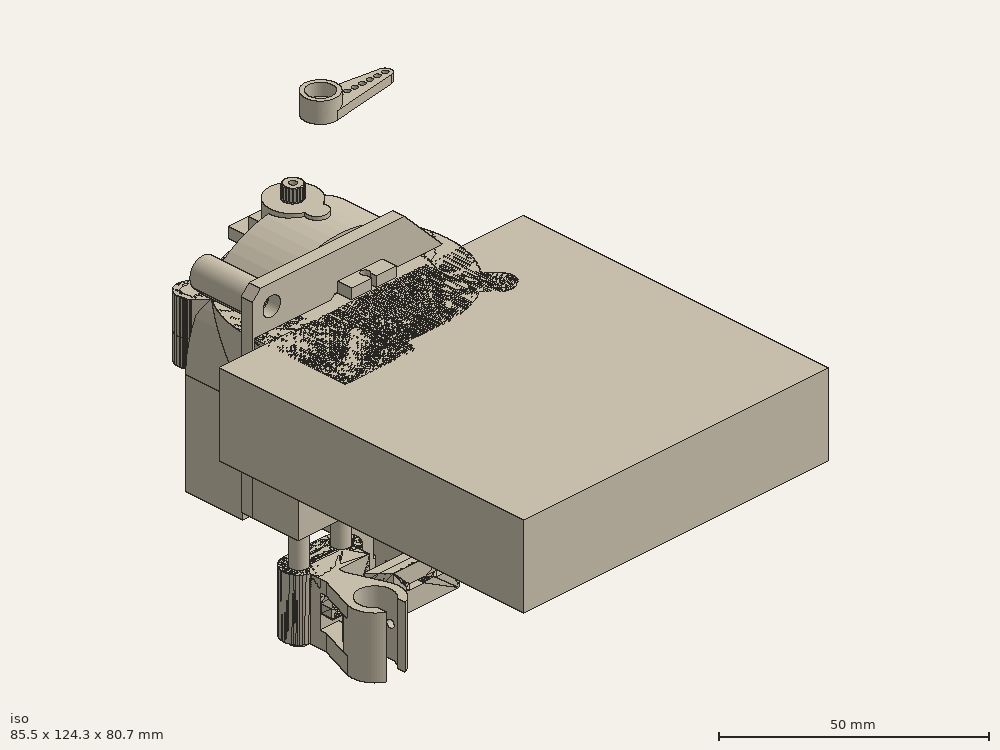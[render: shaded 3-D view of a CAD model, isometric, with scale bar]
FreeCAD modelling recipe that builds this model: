
FCSTD DOCUMENT  (FreeCAD 0.17R13522 (Git))
Label: plotter
License: All rights reserved
LicenseURL: http://en.wikipedia.org/wiki/All_rights_reserved
objects: Part::Box×15, Part::Cylinder×15, App::DocumentObjectGroup×11, Part::Cut×11, PartDesign::ShapeBinder×7, Part::Fuse×7, Sketcher::SketchObject×7, Part::MultiFuse×7, Part::Feature×6, Part::Chamfer×6, PartDesign::Point×5, Part::Part2DObjectPython×4, PartDesign::Pocket×4, Mesh::Feature×3, PartDesign::Pad×3, Part::Fillet×2, PartDesign::Body×2, Part::Compound×1, Spreadsheet::Sheet×1, Part::FeaturePython×1, +1 more types
note: 111 computed .brp shape members not serialized (recipe doc carries the construction recipe); baked Part::Feature solids carry a one-line shape summary decoded from their .brp

FEATURE [Part::Feature] Part__Feature  label="TFD-B5015 TITAN"
  Placement = pos=(0,0,7.5) rot=(0,0,1;0rad)
  shape: bbox 51.8 x 51.1 x 15 mm, 65 faces (baked)
FEATURE [Part::Feature] Part__Feature001  label="TFD-B5015 TITAN001"
  shape: bbox 43 x 43 x 11.5 mm, 91 faces (baked)
FEATURE [Part::Part2DObjectPython] Line  # Draft 2D object (typed FeaturePython)
  ChamferSize = 0
  Closed = false
  End = (0,0,10.5)
  FilletRadius = 0
  MakeFace = false
  MapMode = 5
  Points = (2) [(-2.07596,14.8557,11),(0,0,10.5)]
  Start = (-2.07596,14.8557,11)
  Support = -> [Part__Feature001]
FEATURE [Part::Part2DObjectPython] Line001  # Draft 2D object (typed FeaturePython)
  ChamferSize = 0
  Closed = false
  End = (4.6539,11.0608,10.5)
  FilletRadius = 0
  MakeFace = false
  MapMode = 5
  Points = (2) [(0,0,10.5),(4.6539,11.0608,10.5)]
  Start = (0,0,10.5)
  Support = -> [Part__Feature001]
FEATURE [Part::Fillet] Fillet
  Edges = 1 edges r=1: [Edge57]
FEATURE [App::DocumentObjectGroup] Group  label="Inner-part-src"
  Group = -> [Fillet]
FEATURE [Part::Feature] Fillet001  label="Inner-part-final"
  shape: bbox 43 x 43 x 11.5 mm, 153 faces (baked)
FEATURE [Part::Part2DObjectPython] Line002  # Draft 2D object (typed FeaturePython)
  ChamferSize = 0
  Closed = false
  End = (19.4,-18.3,15)
  FilletRadius = 0
  MakeFace = false
  MapMode = 5
  Points = (2) [(0,0,15),(19.4,-18.3,15)]
  Start = (0,0,15)
  Support = -> [Part__Feature]
FEATURE [Part::Part2DObjectPython] Line003  # Draft 2D object (typed FeaturePython)
  ChamferSize = 0
  Closed = false
  End = (-23.2,20.1,15)
  FilletRadius = 0
  MakeFace = false
  MapMode = 5
  Points = (2) [(0,0,15),(-23.2,20.1,15)]
  Start = (0,0,15)
  Support = -> [Part__Feature]
FEATURE [App::DocumentObjectGroup] Construction
  Group = -> [Line,Line001,Line002,Line003]
FEATURE [Part::Cut] Cut  label="cover-1"
  Refine = true
FEATURE [App::DocumentObjectGroup] Group001  label="cover-src"
  Group = -> [Cut]
FEATURE [Part::Feature] Pad005001  label="cover-final"
  Placement = pos=(0,0,-2) rot=(0,0,1;0rad)
  shape: bbox 51.8 x 51 x 15 mm, 33 faces (baked)
FEATURE [Part::Compound] Compound  label="Blower-50x50-final"
  Links = -> [Fillet001,Pad005001]
  Placement = pos=(0,15,0) rot=(1,0,0;1.5708rad)
FEATURE [App::DocumentObjectGroup] Group002  label="Blower"
  Group = -> [Part__Feature,Part__Feature001,Construction,Group,Group001,Compound]
FEATURE [Mesh::Feature] original
FEATURE [Part::Box] Box  label="Cubo"
  AttacherType = Attacher::AttachEngine3D
  Height = 20
  Length = 80
  Placement = pos=(-40,-84,-5) rot=(0,0,1;0rad)
  Width = 80
FEATURE [Mesh::Feature] difference
FEATURE [Mesh::Feature] union
  Placement = pos=(-23,50.7,-49.11) rot=(0,0,1;3.14159rad)
FEATURE [App::DocumentObjectGroup] Group003  label="Fan duct"
  Group = -> [original,Box,difference,union]
FEATURE [PartDesign::ShapeBinder] CopyCompound
  Placement = pos=(0,2,0) rot=(1,0,0;1.5708rad)
FEATURE [PartDesign::Point] DatumPoint  label="DatumPoint_MainScrew1"
  AttacherType = Attacher::AttachEnginePoint
  MapMode = 36
  Placement = pos=(-23.2,2,20.1) rot=(1,0,0;3.14159rad)
  Support = -> [CopyCompound]
FEATURE [PartDesign::ShapeBinder] CopyCompound001
  Placement = pos=(0,2,0) rot=(1,0,0;1.5708rad)
FEATURE [PartDesign::Point] DatumPoint001  label="DatumPoint_MainScrew2"
  AttacherType = Attacher::AttachEnginePoint
  MapMode = 36
  Placement = pos=(19.4,2,-18.3) rot=(1,0,0;3.14159rad)
  Support = -> [CopyCompound001]
FEATURE [Spreadsheet::Sheet] Spreadsheet
  cells = A2=Fan hole diameter; B2(fanHoleDiam)=32; A3=Fan support thickness; B3(FanSuppThick)=3; A4=Fan support width; B4(FanSuppWidth)=10; A5=Shaft thickness; B5(shaftThick)=4; A6=Left Shaft length; B6(shaftLength)=50; A7=Right shaft length; B7(shaftLengthRight)=33; A9=Shaft Axis X position; B9(AxisX)==-Spreadsheet.FanSuppWidth - 13; A10=Shaft Axis Y position; B10(AxisY)=-8; A12=Shaft Axis tolerance; B12(AxisTolerance)=0.20000000000000001; A13=Shaft Axis separation; B13(AxisSeparation)=11; A15=Servo Connecting Rod Flexible Part Thickness; B15(FlexThickness)=0.80000000000000004; A18=Agrandar el prisionero de M2 a M3; A19=Tornillos soporte principal M3; A20=Modificar parte flexible al doble de tamaño
FEATURE [Part::Box] Box001  label="Cubo001"
  AttacherType = Attacher::AttachEngine3D
  Height = 22.7
  Length = 11.8
  Width = 22.5
FEATURE [Part::Box] Box002  label="Cubo002"
  AttacherType = Attacher::AttachEngine3D
  Height = 2.5
  Length = 11.8
  Placement = pos=(0,-4.7,15.9) rot=(0,0,1;0rad)
  Width = 32.4
FEATURE [Part::Fuse] Fusion  label="Square_body"
  Base = -> Box001
  Refine = true
  Tool = -> Box002
FEATURE [Part::Cylinder] Cylinder  label="Cilindro"
  Angle = 360
  AttacherType = Attacher::AttachEngine3D
  Height = 4
  Placement = pos=(5.9,16.6,22.7) rot=(0,0,1;0rad)
  Radius = 5.9
FEATURE [Part::Cylinder] Cylinder001  label="Cilindro001"
  Angle = 360
  AttacherType = Attacher::AttachEngine3D
  Height = 4
  Placement = pos=(5.9,10.3,22.7) rot=(0,0,1;0rad)
  Radius = 2.5
FEATURE [Part::Fuse] Fusion001
  Base = -> Cylinder
  Refine = true
  Tool = -> Cylinder001
FEATURE [Part::Fuse] Fusion003
  Base = -> Fusion
  Refine = true
  Tool = -> Fusion001
FEATURE [Part::Cylinder] Cylinder003  label="Taladro"
  Angle = 360
  AttacherType = Attacher::AttachEngine3D
  Height = 10
  Placement = pos=(5.9,-2.35,11) rot=(0,0,1;0rad)
  Radius = 1
FEATURE [Part::Cylinder] Cylinder004  label="Taladro2"
  Angle = 360
  AttacherType = Attacher::AttachEngine3D
  Height = 10
  Placement = pos=(5.9,24.85,11) rot=(0,0,1;0rad)
  Radius = 1
FEATURE [Part::Fuse] Fusion004  label="Taladros"
  Base = -> Cylinder003
  Refine = true
  Tool = -> Cylinder004
FEATURE [Part::Box] Box003  label="Cubo003"
  AttacherType = Attacher::AttachEngine3D
  Height = 10
  Length = 1.3
  Placement = pos=(5.25,-6,12) rot=(0,0,1;0rad)
  Width = 3.3
FEATURE [Part::Box] Box004  label="Cubo004"
  AttacherType = Attacher::AttachEngine3D
  Height = 10
  Length = 1.3
  Placement = pos=(5.25,25,12) rot=(0,0,1;0rad)
  Width = 3.3
FEATURE [Part::Fuse] Fusion005  label="Rebajes"
  Base = -> Box003
  Refine = true
  Tool = -> Box004
FEATURE [Part::Fuse] Fusion006  label="Taladros001"
  Base = -> Fusion004
  Refine = true
  Tool = -> Fusion005
FEATURE [Part::Cut] Cut001  label="Cuerpo_con_taladros"
  Base = -> Fusion003
  Placement = pos=(-5.9,0,0) rot=(0,0,1;0rad)
  Refine = true
  Tool = -> Fusion006
FEATURE [Part::Cylinder] Cylinder006  label="Cilindro002"
  Angle = 360
  AttacherType = Attacher::AttachEngine3D
  Height = 3
  Placement = pos=(2.51021,16.5511,26.9) rot=(0,0,1;0rad)
  Radius = 0.35
FEATURE [Part::FeaturePython] Array  # Draft array (typed FeaturePython)
  Angle = 360
  ArrayType = 1
  Axis = (0,0,1)
  Base = -> Cylinder006
  Center = (0,16.6,0)
  Fuse = false
  IntervalAxis = (0,0,0)
  IntervalX = (1,0,0)
  IntervalY = (0,1,0)
  IntervalZ = (0,0,0)
  NumberPolar = 20
  NumberX = 2
  NumberY = 2
  NumberZ = 1
FEATURE [Part::Cylinder] Cylinder002  label="Cilindro_interior"
  Angle = 360
  AttacherType = Attacher::AttachEngine3D
  Height = 3.2
  Placement = pos=(0,16.6,26.7) rot=(0,0,1;0rad)
  Radius = 2.3
FEATURE [Part::Cylinder] Cylinder005  label="Cilindro_exterior"
  Angle = 360
  AttacherType = Attacher::AttachEngine3D
  Height = 3.2
  Placement = pos=(0,16.6,26.7) rot=(0,0,1;0rad)
  Radius = 0.85
FEATURE [Part::Cut] Cut002  label="Cilindro_vaciado"
  Base = -> Cylinder002
  Refine = true
  Tool = -> Cylinder005
FEATURE [Part::Fillet] Fillet002
  Base = -> Cut002
  Edges = 1 edges r=0.3: [Edge1]
FEATURE [Part::Cut] Cut003  label="Eje_engranaje"
  Base = -> Fillet002
  Refine = true
  Tool = -> Array
FEATURE [Part::Feature] Fusion007001  label="Servo-sg90-final"
  Placement = pos=(10,14.9,-22) rot=(0,0.707107,-0.707107;3.14159rad)
  shape: bbox 11.8 x 29.9 x 32.4 mm, 77 faces (baked)
  expr: Placement.Base.y = 17.899999999999999 - Spreadsheet.FanSuppThick
FEATURE [App::DocumentObjectGroup] Grupo003  label="Servo"
  Group = -> [Cut001,Cut003,Fusion007001]
FEATURE [Part::Fuse] Fusion008
  Placement = pos=(26.9697,36.3362,25.6722) rot=(0,0,1;0rad)
  Refine = true
FEATURE [App::DocumentObjectGroup] Grupo001  label="1-arm-horn"
  Group = -> [Fusion008]
FEATURE [Part::Feature] Pocket002001  label="Final-1-arm-horn"
  Placement = pos=(9.96971,-16.96,-38.6278) rot=(0,0.707107,0.707107;3.14159rad)
  shape: bbox 22.5 x 5 x 8 mm, 19 faces (baked)
  expr: Placement.Base.y = -13.960000000000001 - Spreadsheet.FanSuppThick
FEATURE [App::DocumentObjectGroup] Group004  label="ServoArm"
  Group = -> [Grupo001,Pocket002001]
FEATURE [PartDesign::ShapeBinder] CopyFusion007001
FEATURE [PartDesign::Point] DatumPoint002  label="DatumPoint_ServoHeight"
  AttacherType = Attacher::AttachEnginePoint
  MapMode = 37
  Placement = pos=(15.9,-8.8,-22) rot=(0,0,1;0rad)
  Support = -> [CopyFusion007001]
FEATURE [PartDesign::ShapeBinder] CopyFusion007001001
  Placement = pos=(15.9,13.9,-22) rot=(0,0.707107,-0.707107;3.14159rad)
FEATURE [PartDesign::Point] DatumPoint003  label="DatumPoint_ServoScrew1"
  AttacherType = Attacher::AttachEnginePoint
  MapMode = 36
  Placement = pos=(10,-4.5,-19.65) rot=(0,0,1;3.14159rad)
  Support = -> [CopyFusion007001001]
FEATURE [PartDesign::ShapeBinder] CopyFusion007001002
  Placement = pos=(15.9,13.9,-22) rot=(0,0.707107,-0.707107;3.14159rad)
FEATURE [PartDesign::Point] DatumPoint004  label="DatumPoint_ServoScrew2"
  AttacherType = Attacher::AttachEnginePoint
  MapMode = 36
  Placement = pos=(10,-4.5,-46.85) rot=(0.908295,0,-0.41833;3.14159rad)
  Support = -> [CopyFusion007001002]
FEATURE [Sketcher::SketchObject] Sketch  label="Sketch_SupportBase"
  ExternalGeometry = -> [DatumPoint,DatumPoint001,DatumPoint002,DatumPoint003,DatumPoint004]
  MapMode = 5
  Placement = pos=(0,0,0) rot=(1,0,0;1.5708rad)
  Support = -> [XZ_Plane]
  expr: Constraints[3] = 0.5 * Spreadsheet.FanSuppWidth
  expr: Constraints[34] = Spreadsheet.fanHoleDiam * 0.5
  expr: Constraints[4] = 0.5 * Spreadsheet.FanSuppWidth
  expr: Constraints[71] = 0.5 * Spreadsheet.FanSuppWidth
  expr: Constraints[72] = 0.5 * Spreadsheet.FanSuppWidth
  sketch-geometry (29):
    g0: LineSegment StartX=-26.0787 StartY=25.1 StartZ=0 EndX=11.6721 EndY=25.1 EndZ=0
    g1: LineSegment StartX=24.4 StartY=12.3721 StartZ=0 EndX=24.4 EndY=-23.3 EndZ=0
    g2: LineSegment StartX=-28.2 StartY=-23.3 StartZ=0 EndX=-28.2 EndY=22.9787 EndZ=0
    g3: Circle CenterX=-23.2 CenterY=20.1 CenterZ=0 NormalX=0 NormalY=0 NormalZ=1 AngleXU=0 Radius=2.3
    g4: Circle CenterX=19.4 CenterY=-18.3 CenterZ=0 NormalX=0 NormalY=0 NormalZ=1 AngleXU=0 Radius=2.3
    g5: LineSegment StartX=16 StartY=6.62742 StartZ=0 EndX=6.62742 EndY=16 EndZ=0
    g6: LineSegment StartX=6.62742 StartY=16 StartZ=0 EndX=-6.62742 EndY=16 EndZ=0
    g7: LineSegment StartX=-6.62742 StartY=16 StartZ=0 EndX=-16 EndY=6.62742 EndZ=0
    g8: LineSegment StartX=-16 StartY=6.62742 StartZ=0 EndX=-16 EndY=-6.62742 EndZ=0
    g9: LineSegment StartX=-16 StartY=-6.62742 StartZ=0 EndX=-6.62742 EndY=-16 EndZ=0
    g10: LineSegment StartX=-6.62742 StartY=-16 StartZ=0 EndX=6.62742 EndY=-16 EndZ=0
    g11: LineSegment StartX=6.62742 StartY=-16 StartZ=0 EndX=16 EndY=-6.62742 EndZ=0
    g12: LineSegment StartX=16 StartY=-6.62742 StartZ=0 EndX=16 EndY=6.62742 EndZ=0
    g13: Circle [constr] CenterX=0 CenterY=0 CenterZ=0 NormalX=0 NormalY=0 NormalZ=1 AngleXU=0 Radius=17.3183
    g14: LineSegment StartX=16.9 StartY=-50 StartZ=0 EndX=-0.551549 EndY=-50 EndZ=0
    g15: LineSegment StartX=-7.74282 StartY=-23.3 StartZ=0 EndX=-28.2 EndY=-23.3 EndZ=0
    g16: Circle CenterX=10.0164 CenterY=-19.6473 CenterZ=0 NormalX=0 NormalY=0 NormalZ=1 AngleXU=0 Radius=1
    g17: LineSegment StartX=16.9 StartY=-50 StartZ=0 EndX=24.4 EndY=-42.5 EndZ=0
    g18: LineSegment StartX=24.4 StartY=-23.3 StartZ=0 EndX=24.4 EndY=-42.5 EndZ=0
    g19: LineSegment StartX=-2.67287 StartY=-28.37 StartZ=0 EndX=-2.67287 EndY=-47.8787 EndZ=0
    g20: LineSegment StartX=-2.67287 StartY=-47.8787 StartZ=0 EndX=-0.551549 EndY=-50 EndZ=0
    g21: LineSegment StartX=3.5 StartY=-21.4 StartZ=0 EndX=16.5 EndY=-21.4 EndZ=0
    g22: LineSegment StartX=16.5 StartY=-21.4 StartZ=0 EndX=16.5 EndY=-45 EndZ=0
    g23: LineSegment StartX=16.5 StartY=-45 StartZ=0 EndX=3.5 EndY=-45 EndZ=0
    g24: LineSegment StartX=3.5 StartY=-45 StartZ=0 EndX=3.5 EndY=-21.4 EndZ=0
    g25: Circle CenterX=10 CenterY=-46.85 CenterZ=0 NormalX=0 NormalY=0 NormalZ=1 AngleXU=0 Radius=1.2
    g26: LineSegment StartX=11.6721 StartY=25.1 StartZ=0 EndX=24.4 EndY=12.3721 EndZ=0
    g27: LineSegment StartX=-26.0787 StartY=25.1 StartZ=0 EndX=-28.2 EndY=22.9787 EndZ=0
    g28: LineSegment StartX=-2.67287 StartY=-28.37 StartZ=0 EndX=-7.74282 EndY=-23.3 EndZ=0
  constraints (75):
    c: Horizontal(g0)
    c: Vertical(g1)
    c: Vertical(g2)
    c: DistanceY(g1,g-4) = 5
    c: DistanceX(g-4,g1) = 5
    c: Coincident(g3,g-3)
    c: Radius(g3) = 2.3
    c: Coincident(g4,g-4)
    c: Radius(g4) = 2.3
    c: Coincident(g5,g6)
    c: Coincident(g6,g7)
    c: Coincident(g7,g8)
    c: Coincident(g8,g9)
    c: Coincident(g9,g10)
    c: Coincident(g10,g11)
    c: Coincident(g11,g12)
    c: Coincident(g12,g5)
    c: Equal(g5, g6-g12) x7
    c: PointOnObject(g5,g13)
    c: PointOnObject(g6,g13)
    c: PointOnObject(g7,g13)
    c: PointOnObject(g8,g13)
    c: PointOnObject(g9,g13)
    c: PointOnObject(g10,g13)
    c: PointOnObject(g11,g13)
    c: PointOnObject(g12,g13)
    c: Coincident(g13,g-1)
    c: Horizontal(g6)
    c: DistanceY(g-1,g5) = 16
    c: DistanceY(g-5,g14) = -28
    c: Horizontal(g14)
    c: DistanceX(g-5,g14) = 1
    c: Coincident(g15,g2)
    c: Radius(g16) = 1.2
    c: Block(g16)
    c: Coincident(g17,g14)
    c: Coincident(g18,g17)
    c: Vertical(g18)
    c: Angle(g18,g17) = 2.35619
    c: Vertical(g19)
    c: Coincident(g19,g20)
    c: Coincident(g20,g14)
    c: Angle(g20,g19) = 2.35619
    c: Coincident(g21,g22)
    c: Coincident(g22,g23)
    c: Coincident(g23,g24)
    c: Coincident(g24,g21)
    c: Horizontal(g21)
    c: Horizontal(g23)
    c: Vertical(g22)
    c: Vertical(g24)
    c: DistanceX(g-5,g21) = 0.6
    c: DistanceY(g-5,g21) = 0.6
    c: DistanceX(g23,g21) = 13
    c: DistanceY(g23,g21) = 23.6
    c: Horizontal(g15)
    c: PointOnObject(g1,g15)
    c: Coincident(g25,g-7)
    c: Radius(g25) = 1.2
    c: Coincident(g0,g26)
    c: Coincident(g26,g1)
    c: Angle(g0,g26) = 2.35619
    c: Distance(g26) = 18
    c: Coincident(g2,g27)
    c: Coincident(g0,g27)
    c: DistanceX(g2,g3) = 5
    c: DistanceY(g3,g0) = 5
    c: Distance(g27) = 3
    c: Angle(g27,g0) = 2.35619
    c: Coincident(g18,g1)
    c: Distance(g20) = 3
    c: Coincident(g15,g28)
    c: Coincident(g28,g19)
    c: Angle(g15,g28) = 2.35619
    c: Distance(g28) = 7.17
FEATURE [PartDesign::Pad] Pad
  Length = 3
  Length2 = 100
  Placement = pos=(0,0,0) rot=(1,0,0;1.5708rad)
  Profile = -> Sketch
  Type = 0
  expr: Length = Spreadsheet.FanSuppThick
FEATURE [Sketcher::SketchObject] Sketch001  label="Sketch_AxisSupport"
  ExternalGeometry = -> [Pad]
  MapMode = 5
  Placement = pos=(0,-3,0) rot=(1,0,0;1.5708rad)
  Support = -> [Pad]
  sketch-geometry (8):
    g0: LineSegment StartX=-26.0787 StartY=4.82132 StartZ=0 EndX=-20.1213 EndY=4.82132 EndZ=0
    g1: LineSegment StartX=-18 StartY=2.7 StartZ=0 EndX=-20.1213 EndY=4.82132 EndZ=0
    g2: LineSegment StartX=-26.0787 StartY=4.82132 StartZ=0 EndX=-28.2 EndY=2.7 EndZ=0
    g3: LineSegment StartX=-18 StartY=2.7 StartZ=0 EndX=-18 EndY=-6.62742 EndZ=0
    g4: LineSegment StartX=-18 StartY=-6.62742 StartZ=0 EndX=-6.62742 EndY=-18 EndZ=0
    g5: LineSegment StartX=-6.62742 StartY=-18 StartZ=0 EndX=-6.62742 EndY=-23.3 EndZ=0
    g6: LineSegment StartX=-6.62742 StartY=-23.3 StartZ=0 EndX=-28.2 EndY=-23.3 EndZ=0
    g7: LineSegment StartX=-28.2 StartY=-23.3 StartZ=0 EndX=-28.2 EndY=2.7 EndZ=0
  constraints (23):
    c: Horizontal(g0)
    c: Coincident(g1,g0)
    c: Coincident(g0,g2)
    c: Angle(g2,g0) = 2.35619
    c: Angle(g0,g1) = 2.35619
    c: Equal(g1,g2)
    c: Distance(g1) = 3
    c: Vertical(g3)
    c: Coincident(g3,g4)
    c: Coincident(g4,g5)
    c: Vertical(g5)
    c: Coincident(g5,g6)
    c: Coincident(g6,g-3)
    c: Horizontal(g6)
    c: Coincident(g6,g7)
    c: Vertical(g7)
    c: Coincident(g7,g2)
    c: Coincident(g3,g1)
    c: PointOnObject(g-4,g5)
    c: DistanceY(g4,g-4) = 2
    c: DistanceX(g3,g-4) = 2
    c: Angle(g4,g3) = 2.35619
    c: DistanceY(g6,g2) = 26
FEATURE [Part::Cylinder] Cylinder007  label="ShaftLeft"
  Angle = 360
  AttacherType = Attacher::AttachEngine3D
  Height = 50
  Placement = pos=(-23,-8,-49) rot=(0,0,1;0rad)
  Radius = 2
  expr: Placement.Base.y = Spreadsheet.AxisY
  expr: Placement.Base.x = Spreadsheet.AxisX
  expr: Height = Spreadsheet.shaftLength
  expr: Radius = Spreadsheet.shaftThick * 0.5
FEATURE [PartDesign::Pad] Pad005002
  BaseFeature = -> Pad
  Length = 12
  Length2 = 100
  Placement = pos=(0,0,0) rot=(1,0,0;1.5708rad)
  Profile = -> Sketch001
  Type = 0
FEATURE [Part::Cylinder] Cylinder008  label="ShaftRight"
  Angle = 360
  AttacherType = Attacher::AttachEngine3D
  Height = 33
  Placement = pos=(-12,-8,-49) rot=(0,0,1;0rad)
  Radius = 2
  expr: Placement.Base.y = Spreadsheet.AxisY
  expr: Placement.Base.x = Spreadsheet.AxisX + Spreadsheet.AxisSeparation
  expr: Height = Spreadsheet.shaftLengthRight
  expr: Radius = Spreadsheet.shaftThick * 0.5
FEATURE [Sketcher::SketchObject] Sketch002  label="Sketch_AxisLeftHole"
  AttachmentOffset = pos=(24,0,-28.2) rot=(0,1,0;1.5708rad)
  MapMode = 5
  Placement = pos=(0,2e-12,-24) rot=(1,0,0;3.14159rad)
  Support = -> [Pad005002]
  expr: Constraints[4] = 2.1499999999999999
  expr: Constraints[3] = Spreadsheet.AxisSeparation
  expr: Constraints[1] = -Spreadsheet.AxisY + 2
  expr: Constraints[0] = -Spreadsheet.AxisX
  sketch-geometry (2):
    g0: Circle CenterX=-23 CenterY=10 CenterZ=0 NormalX=0 NormalY=0 NormalZ=1 AngleXU=0 Radius=2.15
    g1: Circle [constr] CenterX=-12 CenterY=10 CenterZ=0 NormalX=0 NormalY=0 NormalZ=1 AngleXU=0 Radius=2.15
  constraints (6):
    c: DistanceX(g0,g-1) = 23
    c: DistanceY(g-1,g0) = 10
    c: DistanceY(g1,g0) = 0
    c: DistanceX(g0,g1) = 11
    c: Radius(g1) = 2.15
    c: Radius(g0) = 2.15
FEATURE [Sketcher::SketchObject] Sketch003  label="Sketch_AxisRightHole"
  AttachmentOffset = pos=(24,0,-28.2) rot=(0,1,0;1.5708rad)
  MapMode = 5
  Placement = pos=(0,2e-12,-24) rot=(1,0,0;3.14159rad)
  Support = -> [Pad005002]
  expr: Constraints[4] = 2.1499999999999999
  expr: Constraints[3] = Spreadsheet.AxisSeparation
  expr: Constraints[1] = -Spreadsheet.AxisY + 2
  expr: Constraints[0] = -Spreadsheet.AxisX
  sketch-geometry (2):
    g0: Circle [constr] CenterX=-23 CenterY=10 CenterZ=0 NormalX=0 NormalY=0 NormalZ=1 AngleXU=0 Radius=2.15
    g1: Circle CenterX=-12 CenterY=10 CenterZ=0 NormalX=0 NormalY=0 NormalZ=1 AngleXU=0 Radius=2.15
  constraints (6):
    c: DistanceX(g0,g-1) = 23
    c: DistanceY(g-1,g0) = 10
    c: DistanceY(g1,g0) = 0
    c: DistanceX(g0,g1) = 11
    c: Radius(g1) = 2.15
    c: Radius(g0) = 2.15
FEATURE [PartDesign::Pocket] Pocket
  BaseFeature = -> Pad005002
  Length = 24
  Length2 = 100
  Placement = pos=(0,0,0) rot=(1,0,0;1.5708rad)
  Profile = -> Sketch002
  Type = 0
FEATURE [PartDesign::Pocket] Pocket002002
  BaseFeature = -> Pocket
  Length = 7
  Length2 = 100
  Placement = pos=(0,0,0) rot=(1,0,0;1.5708rad)
  Profile = -> Sketch003
  Type = 0
FEATURE [Sketcher::SketchObject] Sketch004  label="Sketch_ServoCableHole"
  ExternalGeometry = -> [Pocket002002]
  MapMode = 5
  Placement = pos=(0,-3,0) rot=(1,0,0;1.5708rad)
  Support = -> [Pocket002002]
  sketch-geometry (7):
    g0: LineSegment StartX=12.5 StartY=-43.35 StartZ=0 EndX=7.5 EndY=-43.35 EndZ=0
    g1: LineSegment StartX=7.5 StartY=-43.35 StartZ=0 EndX=7.5 EndY=-46.35 EndZ=0
    g2: LineSegment StartX=7.5 StartY=-46.35 StartZ=0 EndX=8 EndY=-46.85 EndZ=0
    g3: LineSegment StartX=12 StartY=-46.85 StartZ=0 EndX=12.5 EndY=-46.35 EndZ=0
    g4: LineSegment StartX=12.5 StartY=-46.35 StartZ=0 EndX=12.5 EndY=-43.35 EndZ=0
    g5: LineSegment StartX=8 StartY=-46.85 StartZ=0 EndX=10 EndY=-46.85 EndZ=0
    g6: LineSegment StartX=10 StartY=-46.85 StartZ=0 EndX=12 EndY=-46.85 EndZ=0
  constraints (20):
    c: Horizontal(g0)
    c: Coincident(g0,g1)
    c: Vertical(g1)
    c: Coincident(g1,g2)
    c: Coincident(g3,g4)
    c: Coincident(g4,g0)
    c: Vertical(g4)
    c: Equal(g2,g3)
    c: Coincident(g5,g2)
    c: Coincident(g5,g-3)
    c: Horizontal(g5)
    c: Coincident(g6,g5)
    c: Coincident(g6,g3)
    c: Equal(g6,g5)
    c: Horizontal(g6)
    c: Equal(g4,g1)
    c: DistanceX(g0,g0) = 5
    c: DistanceX(g6,g6) = 2
    c: Angle(g3,g6) = 2.35619
    c: DistanceY(g4,g4) = 3
FEATURE [PartDesign::Pocket] Pocket002003
  BaseFeature = -> Pocket002002
  Length = 5
  Length2 = 100
  Placement = pos=(0,0,0) rot=(1,0,0;1.5708rad)
  Profile = -> Sketch004
  Type = 1
FEATURE [PartDesign::Body] Body  label="Part 1 - MainSupportPart"
  Group = -> [Sketch,DatumPoint,CopyCompound,DatumPoint001,CopyCompound001,DatumPoint002,CopyFusion007001,DatumPoint003,CopyFusion007001001,DatumPoint004,CopyFusion007001002,Pad,Sketch001,Pad005002,Sketch002,Sketch003,Pocket,Pocket002002,Sketch004,Pocket002003]
  Origin = -> Origin
  Placement = pos=(0,2,0) rot=(0,0,1;0rad)
  Tip = -> Pocket002003
FEATURE [PartDesign::ShapeBinder] CopyBox005
  Placement = pos=(-11,-11,-47.5) rot=(0,0,1;3.14159rad)
FEATURE [Sketcher::SketchObject] Sketch005  label="SketchShaftTubes"
  ExternalGeometry = -> [CopyBox005]
  MapMode = 5
  Placement = pos=(-11,-11,-47.5) rot=(0,1,0;3.14159rad)
  Support = -> [CopyBox005]
  expr: Constraints[17] = 2 + Spreadsheet.AxisTolerance
  sketch-geometry (8):
    g0: LineSegment [constr] StartX=0 StartY=0 StartZ=0 EndX=6.5 EndY=0 EndZ=0
    g1: LineSegment [constr] StartX=6.5 StartY=0 StartZ=0 EndX=13 EndY=0 EndZ=0
    g2: ArcOfCircle CenterX=1 CenterY=3 CenterZ=0 NormalX=0 NormalY=0 NormalZ=1 AngleXU=0 Radius=4 StartAngle=1.5708 EndAngle=4.71239
    g3: ArcOfCircle CenterX=12 CenterY=3 CenterZ=0 NormalX=0 NormalY=0 NormalZ=1 AngleXU=0 Radius=4 StartAngle=4.71239 EndAngle=7.85398
    g4: LineSegment StartX=1 StartY=-1 StartZ=0 EndX=12 EndY=-1 EndZ=0
    g5: LineSegment StartX=1 StartY=7 StartZ=0 EndX=12 EndY=7 EndZ=0
    g6: Circle CenterX=1 CenterY=3 CenterZ=0 NormalX=0 NormalY=0 NormalZ=1 AngleXU=0 Radius=2.2
    g7: Circle CenterX=12 CenterY=3 CenterZ=0 NormalX=0 NormalY=0 NormalZ=1 AngleXU=0 Radius=2.2
  constraints (19):
    c: Coincident(g0,g-1)
    c: Coincident(g1,g0)
    c: Coincident(g1,g-3)
    c: Equal(g0,g1)
    c: Horizontal(g0)
    c: Tangent(g2,g5) = 1.5708
    c: Tangent(g2,g4) = -1.5708
    c: Tangent(g4,g3) = -1.5708
    c: Tangent(g5,g3) = 1.5708
    c: Horizontal(g4)
    c: Equal(g2,g3)
    c: DistanceX(g2,g0) = 5.5
    c: DistanceX(g0,g3) = 5.5
    c: DistanceY(g0,g2) = 3
    c: Radius(g2) = 4
    c: Coincident(g6,g2)
    c: Coincident(g7,g3)
    c: Radius(g7) = 2.2
    c: Equal(g6,g7)
FEATURE [PartDesign::ShapeBinder] CopyBox005001
  Placement = pos=(-11,-11,-47.5) rot=(0,0,1;3.14159rad)
FEATURE [Part::Box] Box005  label="Cube"
  AttacherType = Attacher::AttachEngine3D
  Height = 15
  Length = 13
  Placement = pos=(-11,-11,-47.5) rot=(0,0,1;3.14159rad)
  Width = 3.5
FEATURE [App::DocumentObjectGroup] Group005  label="Printer Parts"
  Group = -> [Group002,Group003,Grupo003,Group004]
FEATURE [Part::Box] Box006  label="Cube001"
  AttacherType = Attacher::AttachEngine3D
  Height = 4
  Length = 5
  Placement = pos=(-24,-23,-47.5) rot=(0,0,1;0rad)
  Width = 11
FEATURE [Part::Box] Box007  label="Cube002"
  AttacherType = Attacher::AttachEngine3D
  Height = 18
  Length = 5
  Placement = pos=(-24,-38,-49) rot=(0,0,1;0rad)
  Width = 11
FEATURE [Part::Cylinder] Cylinder009  label="Cylinder"
  Angle = 360
  AttacherType = Attacher::AttachEngine3D
  Height = 19
  Placement = pos=(-21.5,-26.5,-49.5) rot=(0,0,1;0rad)
  Radius = 4.1
FEATURE [Part::Cylinder] Cylinder010  label="Cylinder001"
  Angle = 360
  AttacherType = Attacher::AttachEngine3D
  Height = 15
  Placement = pos=(-21.5,-26.5,-47.5) rot=(0,0,1;0rad)
  Radius = 6
FEATURE [Part::Box] Box008  label="Cube003"
  AttacherType = Attacher::AttachEngine3D
  Height = 8
  Length = 5
  Placement = pos=(-24,-25.35,-43.5) rot=(0,0,1;0rad)
  Width = 5
FEATURE [Part::Box] Box009  label="Cube004"
  AttacherType = Attacher::AttachEngine3D
  Height = 3
  Length = 5
  Placement = pos=(-24,-23,-35.5) rot=(0,0,1;0rad)
  Width = 11
FEATURE [Part::Cylinder] Cylinder011  label="Cylinder002"
  Angle = 360
  AttacherType = Attacher::AttachEngine3D
  Height = 10
  Placement = pos=(-12.5,-26.5,-40) rot=(0,-1,0;1.5708rad)
  Radius = 0.95
FEATURE [Part::Box] Box010  label="Cube005"
  AttacherType = Attacher::AttachEngine3D
  Height = 5
  Length = 15.5
  Placement = pos=(-24,-17.5,-41.25) rot=(0,0,1;0rad)
  Width = 2.7
FEATURE [Part::Box] Box011  label="Cube006"
  AttacherType = Attacher::AttachEngine3D
  Height = 10
  Length = 21
  Placement = pos=(-15,-21,-44) rot=(0,0,1;0rad)
  Width = 4
FEATURE [Part::Cylinder] Cylinder012  label="Cylinder003"
  Angle = 360
  AttacherType = Attacher::AttachEngine3D
  Height = 10
  Placement = pos=(-3,-14.5,-38.6) rot=(1,0,0;1.5708rad)
  Radius = 0.7
FEATURE [Part::Box] Box012  label="Cube007"
  AttacherType = Attacher::AttachEngine3D
  Height = 1.4
  Length = 4
  Placement = pos=(-7,-24.5,-39.3) rot=(0,0,1;0rad)
  Width = 10
FEATURE [Part::Cylinder] Cylinder013  label="Cylinder004"
  Angle = 360
  AttacherType = Attacher::AttachEngine3D
  Height = 10
  Placement = pos=(-7,-14.5,-38.6) rot=(1,0,0;1.5708rad)
  Radius = 0.7
FEATURE [Part::MultiFuse] Fusion007005
  Placement = pos=(7,0,0) rot=(0,0,1;0rad)
  Refine = true
  Shapes = -> [Cylinder013,Box012,Cylinder012]
FEATURE [Part::MultiFuse] Fusion007006
  Refine = true
  Shapes = -> [Cylinder013,Box012,Cylinder012]
FEATURE [Part::Cut] Cut007
  Base = -> Box011
  Refine = true
  Tool = -> Fusion007006
FEATURE [Part::Cut] Cut008
  Base = -> Cut007
  Refine = true
  Tool = -> Fusion007005
FEATURE [Part::Cylinder] Cylinder014  label="Cylinder005"
  Angle = 360
  AttacherType = Attacher::AttachEngine3D
  Height = 5
  Placement = pos=(-21.5,-13.5,-38.75) rot=(1,0,0;1.5708rad)
  Radius = 1
FEATURE [Part::Cut] Cut009
  Base = -> Box010
  Refine = true
  Tool = -> Cylinder014
FEATURE [Part::Chamfer] Chamfer001
  Base = -> Cut009
  Edges = 2 edges r=1.5: [Edge2,Edge4]
FEATURE [Part::Chamfer] Chamfer002
  Base = -> Chamfer001
  Edges = 2 edges r=1.2: [Edge5,Edge8]
FEATURE [Part::Chamfer] Chamfer003
  Base = -> Cut008
  Edges = 1 edges r=3.8: [Edge1]
FEATURE [Part::MultiFuse] Fusion007007
  Refine = true
  Shapes = -> [Chamfer002,Chamfer003]
FEATURE [Part::Chamfer] Chamfer005  label="ConnectingRod_Without flexible part"
  Base = -> Fusion007007
  Edges = 2 edges r=2: [Edge41,Edge44]
FEATURE [Part::Chamfer] Chamfer004
  Base = -> Fusion007007
  Edges = 2 edges r=0.9: [Edge14,Edge27]
FEATURE [Part::Box] Box013  label="Cube008"
  AttacherType = Attacher::AttachEngine3D
  Height = 2.85
  Length = 3
  Placement = pos=(-19,-19,-42) rot=(0,0,1;0rad)
  Width = 10
  expr: Height = 3.25 - 0.5 * Spreadsheet.FlexThickness
FEATURE [Part::Box] Box014  label="Cube009"
  AttacherType = Attacher::AttachEngine3D
  Height = 3.25
  Length = 3
  Placement = pos=(-19,-19,-38.35) rot=(0,0,1;0rad)
  Width = 10
  expr: Placement.Base.z = -38.75 + 0.5 * Spreadsheet.FlexThickness
  expr: Height = 3.25
FEATURE [Part::MultiFuse] Fusion007008
  Refine = true
  Shapes = -> [Box014,Box013]
FEATURE [Part::Cut] Cut010  label="Final_ConnectingRod"
  Base = -> Chamfer005
  Refine = true
  Tool = -> Fusion007008
FEATURE [App::DocumentObjectGroup] Group007  label="Part 3 - Connecting Rod"
  Group = -> [Chamfer004,Cut010]
FEATURE [PartDesign::Body] Body001  label="SupportPen"
  BaseFeature = -> Fusion007002
  Group = -> [BaseFeature,CopyBox005,Sketch005,Pocket002004,Pad005003,CopyBox005001,Sketch006]
  Origin = -> Origin001
  Tip = -> Pocket002004
FEATURE [PartDesign::Pad] Pad005003
  BaseFeature = -> Pocket002004
  Length = 15
  Length2 = 100
  Profile = -> Sketch005
  Reversed = true
  Type = 0
FEATURE [Part::MultiFuse] Fusion007002
  Refine = true
  Shapes = -> [Pad005003,Box005]
FEATURE [Sketcher::SketchObject] Sketch006  label="Sketch_Groove"
  MapMode = 5
  Placement = pos=(0,-14.5,0) rot=(1,0,0;1.5708rad)
  Support = -> [Fusion007002]
  sketch-geometry (4):
    g0: ArcOfCircle CenterX=-22 CenterY=-38.75 CenterZ=0 NormalX=0 NormalY=0 NormalZ=1 AngleXU=0 Radius=1.25 StartAngle=1.5708 EndAngle=4.71239
    g1: ArcOfCircle CenterX=-13 CenterY=-38.75 CenterZ=0 NormalX=0 NormalY=0 NormalZ=1 AngleXU=0 Radius=1.25 StartAngle=4.71239 EndAngle=7.85398
    g2: LineSegment StartX=-22 StartY=-40 StartZ=0 EndX=-13 EndY=-40 EndZ=0
    g3: LineSegment StartX=-22 StartY=-37.5 StartZ=0 EndX=-13 EndY=-37.5 EndZ=0
  constraints (10):
    c: Tangent(g0,g3) = 1.5708
    c: Tangent(g0,g2) = -1.5708
    c: Tangent(g2,g1) = -1.5708
    c: Tangent(g3,g1) = 1.5708
    c: Horizontal(g2)
    c: Equal(g0,g1)
    c: Radius(g1) = 1.25
    c: DistanceX(g3,g3) = 9
    c: DistanceX(g1,g-1) = 13
    c: DistanceY(g1,g-1) = 37.5
FEATURE [PartDesign::FeatureBase] BaseFeature
  BaseFeature = -> Fusion007002
FEATURE [PartDesign::Pocket] Pocket002004  label="Support1"
  BaseFeature = -> BaseFeature
  Length = 3
  Length2 = 100
  Profile = -> Sketch006
  Type = 0
FEATURE [App::DocumentObjectGroup] Group006  label="Part 2 - Pen Support Example 1"
  Group = -> [Body001,Fusion007002,Cut006]
FEATURE [Part::MultiFuse] Fusion007003
  Refine = true
  Shapes = -> [Pocket002004,Box009,Box006,Cylinder010]
FEATURE [Part::Chamfer] Chamfer
  Base = -> Fusion007003
  Edges = 4 edges r=5: [Edge27,Edge34,Edge45,Edge48]
FEATURE [Part::MultiFuse] Fusion007004
  Refine = true
  Shapes = -> [Box008,Chamfer]
FEATURE [Part::Cut] Cut004
  Base = -> Fusion007004
  Refine = true
  Tool = -> Cylinder009
FEATURE [Part::Cut] Cut005
  Base = -> Cut004
  Refine = true
  Tool = -> Box007
FEATURE [Part::Cut] Cut006  label="Final_PenSupport1"
  Base = -> Cut005
  Refine = true
  Tool = -> Cylinder011
